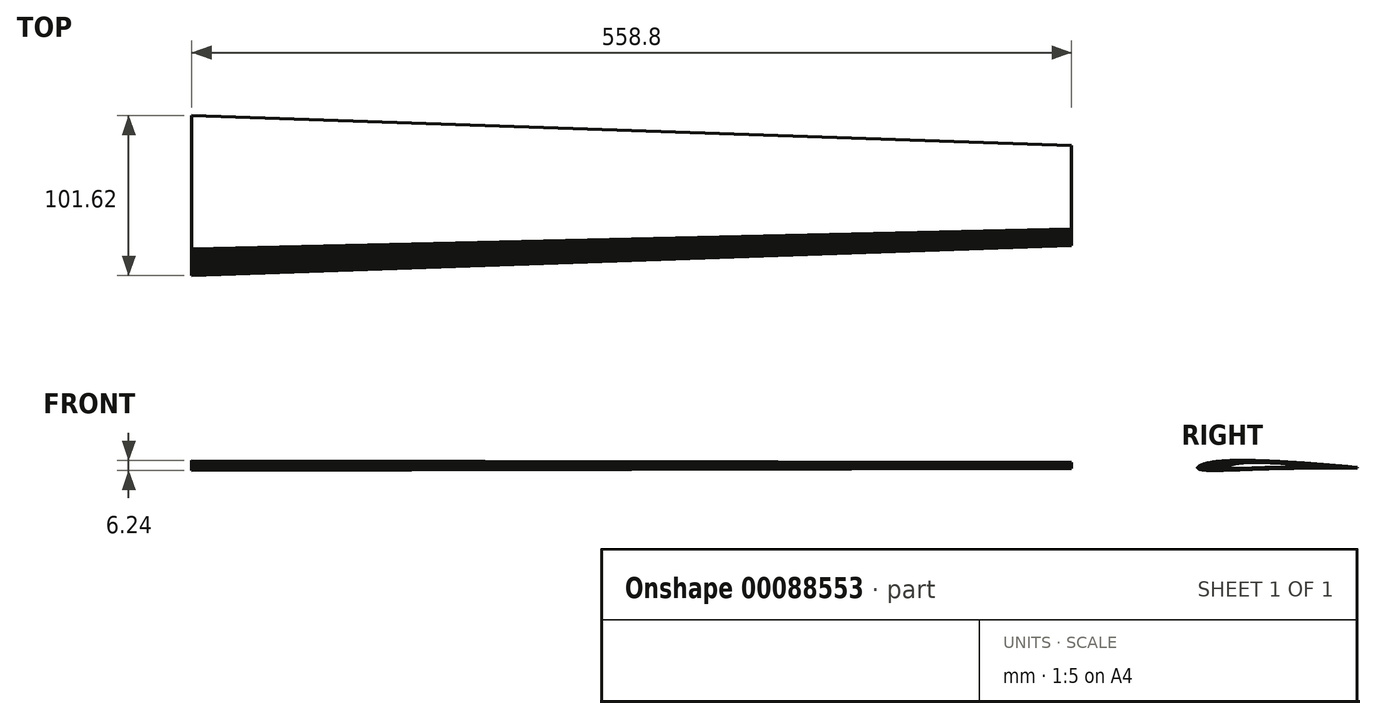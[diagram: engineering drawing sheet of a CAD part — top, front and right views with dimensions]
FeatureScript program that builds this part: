
annotation { "Feature Type Name" : "Feature", "Feature Type Description" : "" }
export const myFeature = defineFeature(function(context is Context, id is Id, definition is map)
    precondition{}
    {
        {
            var Q0;
            Q0=qCreatedBy(makeId("Right.planeOp"),FACE);
            var sketch = newSketch(context, id + "F0", { "sketchPlane" : qUnion([Q0])});
            skLineSegment(sketch, "E0", {"start": v(50.8, -1.4) * mm, "end": v(50.35, -1.36) * mm});
            skLineSegment(sketch, "E1", {"start": v(50.35, -1.36) * mm, "end": v(49.4, -1.27) * mm});
            skLineSegment(sketch, "E2", {"start": v(49.4, -1.27) * mm, "end": v(48.24, -1.16) * mm});
            skLineSegment(sketch, "E3", {"start": v(48.24, -1.16) * mm, "end": v(46.98, -1.04) * mm});
            skLineSegment(sketch, "E4", {"start": v(46.98, -1.04) * mm, "end": v(45.68, -0.91) * mm});
            skLineSegment(sketch, "E5", {"start": v(45.68, -0.91) * mm, "end": v(44.37, -0.8) * mm});
            skLineSegment(sketch, "E6", {"start": v(44.37, -0.8) * mm, "end": v(43.06, -0.67) * mm});
            skLineSegment(sketch, "E7", {"start": v(43.06, -0.67) * mm, "end": v(41.75, -0.55) * mm});
            skLineSegment(sketch, "E8", {"start": v(41.75, -0.55) * mm, "end": v(40.44, -0.43) * mm});
            skLineSegment(sketch, "E9", {"start": v(40.44, -0.43) * mm, "end": v(39.13, -0.32) * mm});
            skLineSegment(sketch, "E10", {"start": v(39.13, -0.32) * mm, "end": v(37.82, -0.2) * mm});
            skLineSegment(sketch, "E11", {"start": v(37.82, -0.2) * mm, "end": v(36.51, -0.1) * mm});
            skLineSegment(sketch, "E12", {"start": v(36.51, -0.1) * mm, "end": v(35.2, 0.02) * mm});
            skLineSegment(sketch, "E13", {"start": v(35.2, 0.02) * mm, "end": v(33.89, 0.13) * mm});
            skLineSegment(sketch, "E14", {"start": v(33.89, 0.13) * mm, "end": v(32.58, 0.24) * mm});
            skLineSegment(sketch, "E15", {"start": v(32.58, 0.24) * mm, "end": v(31.26, 0.35) * mm});
            skLineSegment(sketch, "E16", {"start": v(31.26, 0.35) * mm, "end": v(29.95, 0.45) * mm});
            skLineSegment(sketch, "E17", {"start": v(29.95, 0.45) * mm, "end": v(28.64, 0.56) * mm});
            skLineSegment(sketch, "E18", {"start": v(28.64, 0.56) * mm, "end": v(27.33, 0.66) * mm});
            skLineSegment(sketch, "E19", {"start": v(27.33, 0.66) * mm, "end": v(26.01, 0.76) * mm});
            skLineSegment(sketch, "E20", {"start": v(26.01, 0.76) * mm, "end": v(24.7, 0.87) * mm});
            skLineSegment(sketch, "E21", {"start": v(24.7, 0.87) * mm, "end": v(23.39, 0.96) * mm});
            skLineSegment(sketch, "E22", {"start": v(23.39, 0.96) * mm, "end": v(22.08, 1.06) * mm});
            skLineSegment(sketch, "E23", {"start": v(22.08, 1.06) * mm, "end": v(20.76, 1.16) * mm});
            skLineSegment(sketch, "E24", {"start": v(20.76, 1.16) * mm, "end": v(19.45, 1.25) * mm});
            skLineSegment(sketch, "E25", {"start": v(19.45, 1.25) * mm, "end": v(18.14, 1.35) * mm});
            skLineSegment(sketch, "E26", {"start": v(18.14, 1.35) * mm, "end": v(16.83, 1.44) * mm});
            skLineSegment(sketch, "E27", {"start": v(16.83, 1.44) * mm, "end": v(15.51, 1.53) * mm});
            skLineSegment(sketch, "E28", {"start": v(15.51, 1.53) * mm, "end": v(14.2, 1.62) * mm});
            skLineSegment(sketch, "E29", {"start": v(14.2, 1.62) * mm, "end": v(12.9, 1.7) * mm});
            skLineSegment(sketch, "E30", {"start": v(12.9, 1.7) * mm, "end": v(11.58, 1.8) * mm});
            skLineSegment(sketch, "E31", {"start": v(11.58, 1.8) * mm, "end": v(10.27, 1.88) * mm});
            skLineSegment(sketch, "E32", {"start": v(10.27, 1.88) * mm, "end": v(8.96, 1.96) * mm});
            skLineSegment(sketch, "E33", {"start": v(8.96, 1.96) * mm, "end": v(7.65, 2.04) * mm});
            skLineSegment(sketch, "E34", {"start": v(7.65, 2.04) * mm, "end": v(6.34, 2.12) * mm});
            skLineSegment(sketch, "E35", {"start": v(6.34, 2.12) * mm, "end": v(5.03, 2.2) * mm});
            skLineSegment(sketch, "E36", {"start": v(5.03, 2.2) * mm, "end": v(3.72, 2.26) * mm});
            skLineSegment(sketch, "E37", {"start": v(3.72, 2.26) * mm, "end": v(2.4, 2.33) * mm});
            skLineSegment(sketch, "E38", {"start": v(2.4, 2.33) * mm, "end": v(1.1, 2.4) * mm});
            skLineSegment(sketch, "E39", {"start": v(1.1, 2.4) * mm, "end": v(-0.21, 2.47) * mm});
            skLineSegment(sketch, "E40", {"start": v(-0.21, 2.47) * mm, "end": v(-1.52, 2.53) * mm});
            skLineSegment(sketch, "E41", {"start": v(-1.52, 2.53) * mm, "end": v(-2.83, 2.6) * mm});
            skLineSegment(sketch, "E42", {"start": v(-2.83, 2.6) * mm, "end": v(-4.14, 2.65) * mm});
            skLineSegment(sketch, "E43", {"start": v(-4.14, 2.65) * mm, "end": v(-5.45, 2.7) * mm});
            skLineSegment(sketch, "E44", {"start": v(-5.45, 2.7) * mm, "end": v(-6.76, 2.76) * mm});
            skLineSegment(sketch, "E45", {"start": v(-6.76, 2.76) * mm, "end": v(-8.07, 2.81) * mm});
            skLineSegment(sketch, "E46", {"start": v(-8.07, 2.81) * mm, "end": v(-9.37, 2.86) * mm});
            skLineSegment(sketch, "E47", {"start": v(-9.37, 2.86) * mm, "end": v(-10.68, 2.9) * mm});
            skLineSegment(sketch, "E48", {"start": v(-10.68, 2.9) * mm, "end": v(-11.98, 2.94) * mm});
            skLineSegment(sketch, "E49", {"start": v(-11.98, 2.94) * mm, "end": v(-13.29, 2.98) * mm});
            skLineSegment(sketch, "E50", {"start": v(-13.29, 2.98) * mm, "end": v(-14.6, 3.01) * mm});
            skLineSegment(sketch, "E51", {"start": v(-14.6, 3.01) * mm, "end": v(-15.9, 3.04) * mm});
            skLineSegment(sketch, "E52", {"start": v(-15.9, 3.04) * mm, "end": v(-17.2, 3.07) * mm});
            skLineSegment(sketch, "E53", {"start": v(-17.2, 3.07) * mm, "end": v(-18.5, 3.09) * mm});
            skLineSegment(sketch, "E54", {"start": v(-18.5, 3.09) * mm, "end": v(-19.8, 3.1) * mm});
            skLineSegment(sketch, "E55", {"start": v(-19.8, 3.1) * mm, "end": v(-21.1, 3.12) * mm});
            skLineSegment(sketch, "E56", {"start": v(-21.1, 3.12) * mm, "end": v(-22.39, 3.12) * mm});
            skLineSegment(sketch, "E57", {"start": v(-22.39, 3.12) * mm, "end": v(-23.68, 3.12) * mm});
            skLineSegment(sketch, "E58", {"start": v(-23.68, 3.12) * mm, "end": v(-24.97, 3.12) * mm});
            skLineSegment(sketch, "E59", {"start": v(-24.97, 3.12) * mm, "end": v(-26.25, 3.1) * mm});
            skLineSegment(sketch, "E60", {"start": v(-26.25, 3.1) * mm, "end": v(-27.53, 3.08) * mm});
            skLineSegment(sketch, "E61", {"start": v(-27.53, 3.08) * mm, "end": v(-28.81, 3.05) * mm});
            skLineSegment(sketch, "E62", {"start": v(-28.81, 3.05) * mm, "end": v(-30.09, 3.01) * mm});
            skLineSegment(sketch, "E63", {"start": v(-30.09, 3.01) * mm, "end": v(-31.35, 2.96) * mm});
            skLineSegment(sketch, "E64", {"start": v(-31.35, 2.96) * mm, "end": v(-32.62, 2.9) * mm});
            skLineSegment(sketch, "E65", {"start": v(-32.62, 2.9) * mm, "end": v(-33.88, 2.84) * mm});
            skLineSegment(sketch, "E66", {"start": v(-33.88, 2.84) * mm, "end": v(-35.12, 2.75) * mm});
            skLineSegment(sketch, "E67", {"start": v(-35.12, 2.75) * mm, "end": v(-36.36, 2.66) * mm});
            skLineSegment(sketch, "E68", {"start": v(-36.36, 2.66) * mm, "end": v(-37.6, 2.55) * mm});
            skLineSegment(sketch, "E69", {"start": v(-37.6, 2.55) * mm, "end": v(-38.81, 2.42) * mm});
            skLineSegment(sketch, "E70", {"start": v(-38.81, 2.42) * mm, "end": v(-40.01, 2.28) * mm});
            skLineSegment(sketch, "E71", {"start": v(-40.01, 2.28) * mm, "end": v(-41.2, 2.11) * mm});
            skLineSegment(sketch, "E72", {"start": v(-41.2, 2.11) * mm, "end": v(-42.37, 1.93) * mm});
            skLineSegment(sketch, "E73", {"start": v(-42.37, 1.93) * mm, "end": v(-43.5, 1.72) * mm});
            skLineSegment(sketch, "E74", {"start": v(-43.5, 1.72) * mm, "end": v(-44.61, 1.5) * mm});
            skLineSegment(sketch, "E75", {"start": v(-44.61, 1.5) * mm, "end": v(-45.67, 1.24) * mm});
            skLineSegment(sketch, "E76", {"start": v(-45.67, 1.24) * mm, "end": v(-46.67, 0.96) * mm});
            skLineSegment(sketch, "E77", {"start": v(-46.67, 0.96) * mm, "end": v(-47.57, 0.67) * mm});
            skLineSegment(sketch, "E78", {"start": v(-47.57, 0.67) * mm, "end": v(-48.34, 0.38) * mm});
            skLineSegment(sketch, "E79", {"start": v(-48.34, 0.38) * mm, "end": v(-48.96, 0.1) * mm});
            skLineSegment(sketch, "E80", {"start": v(-48.96, 0.1) * mm, "end": v(-49.44, -0.14) * mm});
            skLineSegment(sketch, "E81", {"start": v(-49.44, -0.14) * mm, "end": v(-49.8, -0.35) * mm});
            skLineSegment(sketch, "E82", {"start": v(-49.8, -0.35) * mm, "end": v(-50.07, -0.54) * mm});
            skLineSegment(sketch, "E83", {"start": v(-50.07, -0.54) * mm, "end": v(-50.28, -0.7) * mm});
            skLineSegment(sketch, "E84", {"start": v(-50.28, -0.7) * mm, "end": v(-50.45, -0.85) * mm});
            skLineSegment(sketch, "E85", {"start": v(-50.45, -0.85) * mm, "end": v(-50.58, -1) * mm});
            skLineSegment(sketch, "E86", {"start": v(-50.58, -1) * mm, "end": v(-50.68, -1.12) * mm});
            skLineSegment(sketch, "E87", {"start": v(-50.68, -1.12) * mm, "end": v(-50.75, -1.24) * mm});
            skLineSegment(sketch, "E88", {"start": v(-50.75, -1.24) * mm, "end": v(-50.8, -1.36) * mm});
            skLineSegment(sketch, "E89", {"start": v(-50.8, -1.36) * mm, "end": v(-50.8, -1.47) * mm});
            skLineSegment(sketch, "E90", {"start": v(-50.8, -1.47) * mm, "end": v(-50.8, -1.57) * mm});
            skLineSegment(sketch, "E91", {"start": v(-50.8, -1.57) * mm, "end": v(-50.77, -1.67) * mm});
            skLineSegment(sketch, "E92", {"start": v(-50.77, -1.67) * mm, "end": v(-50.7, -1.78) * mm});
            skLineSegment(sketch, "E93", {"start": v(-50.7, -1.78) * mm, "end": v(-50.6, -1.9) * mm});
            skLineSegment(sketch, "E94", {"start": v(-50.6, -1.9) * mm, "end": v(-50.47, -2) * mm});
            skLineSegment(sketch, "E95", {"start": v(-50.47, -2) * mm, "end": v(-50.3, -2.1) * mm});
            skLineSegment(sketch, "E96", {"start": v(-50.3, -2.1) * mm, "end": v(-50.1, -2.2) * mm});
            skLineSegment(sketch, "E97", {"start": v(-50.1, -2.2) * mm, "end": v(-49.86, -2.3) * mm});
            skLineSegment(sketch, "E98", {"start": v(-49.86, -2.3) * mm, "end": v(-49.54, -2.4) * mm});
            skLineSegment(sketch, "E99", {"start": v(-49.54, -2.4) * mm, "end": v(-49.14, -2.52) * mm});
            skLineSegment(sketch, "E100", {"start": v(-49.14, -2.52) * mm, "end": v(-48.6, -2.64) * mm});
            skLineSegment(sketch, "E101", {"start": v(-48.6, -2.64) * mm, "end": v(-47.88, -2.76) * mm});
            skLineSegment(sketch, "E102", {"start": v(-47.88, -2.76) * mm, "end": v(-47, -2.87) * mm});
            skLineSegment(sketch, "E103", {"start": v(-47, -2.87) * mm, "end": v(-45.96, -2.97) * mm});
            skLineSegment(sketch, "E104", {"start": v(-45.96, -2.97) * mm, "end": v(-44.84, -3.03) * mm});
            skLineSegment(sketch, "E105", {"start": v(-44.84, -3.03) * mm, "end": v(-43.66, -3.08) * mm});
            skLineSegment(sketch, "E106", {"start": v(-43.66, -3.08) * mm, "end": v(-42.44, -3.1) * mm});
            skLineSegment(sketch, "E107", {"start": v(-42.44, -3.1) * mm, "end": v(-41.2, -3.12) * mm});
            skLineSegment(sketch, "E108", {"start": v(-41.2, -3.12) * mm, "end": v(-39.93, -3.12) * mm});
            skLineSegment(sketch, "E109", {"start": v(-39.93, -3.12) * mm, "end": v(-38.66, -3.11) * mm});
            skLineSegment(sketch, "E110", {"start": v(-38.66, -3.11) * mm, "end": v(-37.37, -3.1) * mm});
            skLineSegment(sketch, "E111", {"start": v(-37.37, -3.1) * mm, "end": v(-36.08, -3.07) * mm});
            skLineSegment(sketch, "E112", {"start": v(-36.08, -3.07) * mm, "end": v(-34.78, -3.05) * mm});
            skLineSegment(sketch, "E113", {"start": v(-34.78, -3.05) * mm, "end": v(-33.47, -3.01) * mm});
            skLineSegment(sketch, "E114", {"start": v(-33.47, -3.01) * mm, "end": v(-32.16, -2.98) * mm});
            skLineSegment(sketch, "E115", {"start": v(-32.16, -2.98) * mm, "end": v(-30.84, -2.94) * mm});
            skLineSegment(sketch, "E116", {"start": v(-30.84, -2.94) * mm, "end": v(-29.52, -2.9) * mm});
            skLineSegment(sketch, "E117", {"start": v(-29.52, -2.9) * mm, "end": v(-28.2, -2.85) * mm});
            skLineSegment(sketch, "E118", {"start": v(-28.2, -2.85) * mm, "end": v(-26.88, -2.8) * mm});
            skLineSegment(sketch, "E119", {"start": v(-26.88, -2.8) * mm, "end": v(-25.56, -2.76) * mm});
            skLineSegment(sketch, "E120", {"start": v(-25.56, -2.76) * mm, "end": v(-24.24, -2.7) * mm});
            skLineSegment(sketch, "E121", {"start": v(-24.24, -2.7) * mm, "end": v(-22.92, -2.66) * mm});
            skLineSegment(sketch, "E122", {"start": v(-22.92, -2.66) * mm, "end": v(-21.6, -2.61) * mm});
            skLineSegment(sketch, "E123", {"start": v(-21.6, -2.61) * mm, "end": v(-20.3, -2.56) * mm});
            skLineSegment(sketch, "E124", {"start": v(-20.3, -2.56) * mm, "end": v(-18.98, -2.51) * mm});
            skLineSegment(sketch, "E125", {"start": v(-18.98, -2.51) * mm, "end": v(-17.67, -2.46) * mm});
            skLineSegment(sketch, "E126", {"start": v(-17.67, -2.46) * mm, "end": v(-16.35, -2.42) * mm});
            skLineSegment(sketch, "E127", {"start": v(-16.35, -2.42) * mm, "end": v(-15.04, -2.37) * mm});
            skLineSegment(sketch, "E128", {"start": v(-15.04, -2.37) * mm, "end": v(-13.73, -2.32) * mm});
            skLineSegment(sketch, "E129", {"start": v(-13.73, -2.32) * mm, "end": v(-12.41, -2.28) * mm});
            skLineSegment(sketch, "E130", {"start": v(-12.41, -2.28) * mm, "end": v(-11.1, -2.24) * mm});
            skLineSegment(sketch, "E131", {"start": v(-11.1, -2.24) * mm, "end": v(-9.79, -2.2) * mm});
            skLineSegment(sketch, "E132", {"start": v(-9.79, -2.2) * mm, "end": v(-8.47, -2.15) * mm});
            skLineSegment(sketch, "E133", {"start": v(-8.47, -2.15) * mm, "end": v(-7.16, -2.11) * mm});
            skLineSegment(sketch, "E134", {"start": v(-7.16, -2.11) * mm, "end": v(-5.85, -2.08) * mm});
            skLineSegment(sketch, "E135", {"start": v(-5.85, -2.08) * mm, "end": v(-4.53, -2.04) * mm});
            skLineSegment(sketch, "E136", {"start": v(-4.53, -2.04) * mm, "end": v(-3.22, -2) * mm});
            skLineSegment(sketch, "E137", {"start": v(-3.22, -2) * mm, "end": v(-1.9, -1.97) * mm});
            skLineSegment(sketch, "E138", {"start": v(-1.9, -1.97) * mm, "end": v(-0.59, -1.94) * mm});
            skLineSegment(sketch, "E139", {"start": v(-0.59, -1.94) * mm, "end": v(0.73, -1.91) * mm});
            skLineSegment(sketch, "E140", {"start": v(0.73, -1.91) * mm, "end": v(2.04, -1.89) * mm});
            skLineSegment(sketch, "E141", {"start": v(2.04, -1.89) * mm, "end": v(3.36, -1.86) * mm});
            skLineSegment(sketch, "E142", {"start": v(3.36, -1.86) * mm, "end": v(4.67, -1.84) * mm});
            skLineSegment(sketch, "E143", {"start": v(4.67, -1.84) * mm, "end": v(6, -1.82) * mm});
            skLineSegment(sketch, "E144", {"start": v(6, -1.82) * mm, "end": v(7.31, -1.8) * mm});
            skLineSegment(sketch, "E145", {"start": v(7.31, -1.8) * mm, "end": v(8.63, -1.78) * mm});
            skLineSegment(sketch, "E146", {"start": v(8.63, -1.78) * mm, "end": v(9.95, -1.76) * mm});
            skLineSegment(sketch, "E147", {"start": v(9.95, -1.76) * mm, "end": v(11.27, -1.74) * mm});
            skLineSegment(sketch, "E148", {"start": v(11.27, -1.74) * mm, "end": v(12.6, -1.73) * mm});
            skLineSegment(sketch, "E149", {"start": v(12.6, -1.73) * mm, "end": v(13.9, -1.72) * mm});
            skLineSegment(sketch, "E150", {"start": v(13.9, -1.72) * mm, "end": v(15.23, -1.7) * mm});
            skLineSegment(sketch, "E151", {"start": v(15.23, -1.7) * mm, "end": v(16.55, -1.7) * mm});
            skLineSegment(sketch, "E152", {"start": v(16.55, -1.7) * mm, "end": v(17.87, -1.69) * mm});
            skLineSegment(sketch, "E153", {"start": v(17.87, -1.69) * mm, "end": v(19.2, -1.68) * mm});
            skLineSegment(sketch, "E154", {"start": v(19.2, -1.68) * mm, "end": v(20.52, -1.67) * mm});
            skLineSegment(sketch, "E155", {"start": v(20.52, -1.67) * mm, "end": v(21.84, -1.67) * mm});
            skLineSegment(sketch, "E156", {"start": v(21.84, -1.67) * mm, "end": v(23.16, -1.66) * mm});
            skLineSegment(sketch, "E157", {"start": v(23.16, -1.66) * mm, "end": v(24.48, -1.66) * mm});
            skLineSegment(sketch, "E158", {"start": v(24.48, -1.66) * mm, "end": v(25.8, -1.65) * mm});
            skLineSegment(sketch, "E159", {"start": v(25.8, -1.65) * mm, "end": v(27.12, -1.65) * mm});
            skLineSegment(sketch, "E160", {"start": v(27.12, -1.65) * mm, "end": v(28.45, -1.64) * mm});
            skLineSegment(sketch, "E161", {"start": v(28.45, -1.64) * mm, "end": v(29.77, -1.64) * mm});
            skLineSegment(sketch, "E162", {"start": v(29.77, -1.64) * mm, "end": v(31.09, -1.63) * mm});
            skLineSegment(sketch, "E163", {"start": v(31.09, -1.63) * mm, "end": v(32.41, -1.63) * mm});
            skLineSegment(sketch, "E164", {"start": v(32.41, -1.63) * mm, "end": v(33.74, -1.63) * mm});
            skLineSegment(sketch, "E165", {"start": v(33.74, -1.63) * mm, "end": v(35.06, -1.62) * mm});
            skLineSegment(sketch, "E166", {"start": v(35.06, -1.62) * mm, "end": v(36.38, -1.62) * mm});
            skLineSegment(sketch, "E167", {"start": v(36.38, -1.62) * mm, "end": v(37.7, -1.62) * mm});
            skLineSegment(sketch, "E168", {"start": v(37.7, -1.62) * mm, "end": v(39.03, -1.61) * mm});
            skLineSegment(sketch, "E169", {"start": v(39.03, -1.61) * mm, "end": v(40.35, -1.6) * mm});
            skLineSegment(sketch, "E170", {"start": v(40.35, -1.6) * mm, "end": v(41.67, -1.6) * mm});
            skLineSegment(sketch, "E171", {"start": v(41.67, -1.6) * mm, "end": v(43, -1.6) * mm});
            skLineSegment(sketch, "E172", {"start": v(43, -1.6) * mm, "end": v(44.32, -1.6) * mm});
            skLineSegment(sketch, "E173", {"start": v(44.32, -1.6) * mm, "end": v(45.64, -1.59) * mm});
            skLineSegment(sketch, "E174", {"start": v(45.64, -1.59) * mm, "end": v(46.95, -1.59) * mm});
            skLineSegment(sketch, "E175", {"start": v(46.95, -1.59) * mm, "end": v(48.22, -1.58) * mm});
            skLineSegment(sketch, "E176", {"start": v(48.22, -1.58) * mm, "end": v(49.4, -1.58) * mm});
            skLineSegment(sketch, "E177", {"start": v(49.4, -1.58) * mm, "end": v(50.35, -1.57) * mm});
            skLineSegment(sketch, "E178", {"start": v(50.35, -1.57) * mm, "end": v(50.8, -1.57) * mm});
            skLineSegment(sketch, "E179", {"start": v(50.8, -1.57) * mm, "end": v(50.8, -1.4) * mm});
            skSolve(sketch);
        }
        {
            var Q0;
            Q0=qCreatedBy(makeId("Right.planeOp"),FACE);
            cPlane(context, id + "F1", {"entities" : qUnion([Q0]), "cplaneType" : CPlaneType.OFFSET, "offset" : 558.8 * mm, "width" : 152.4 * mm, "height" : 152.4 * mm});
        }
        {
            var Q0;
            Q0=qCreatedBy(id+"F1.planeOp",FACE);
            var sketch = newSketch(context, id + "F2", { "sketchPlane" : qUnion([Q0])});
            skLineSegment(sketch, "E180", {"start": v(31.75, -0.88) * mm, "end": v(31.47, -0.85) * mm});
            skLineSegment(sketch, "E181", {"start": v(31.47, -0.85) * mm, "end": v(30.87, -0.8) * mm});
            skLineSegment(sketch, "E182", {"start": v(30.87, -0.8) * mm, "end": v(30.14, -0.72) * mm});
            skLineSegment(sketch, "E183", {"start": v(30.14, -0.72) * mm, "end": v(29.36, -0.65) * mm});
            skLineSegment(sketch, "E184", {"start": v(29.36, -0.65) * mm, "end": v(28.54, -0.57) * mm});
            skLineSegment(sketch, "E185", {"start": v(28.54, -0.57) * mm, "end": v(27.73, -0.5) * mm});
            skLineSegment(sketch, "E186", {"start": v(27.73, -0.5) * mm, "end": v(26.9, -0.42) * mm});
            skLineSegment(sketch, "E187", {"start": v(26.9, -0.42) * mm, "end": v(26.1, -0.35) * mm});
            skLineSegment(sketch, "E188", {"start": v(26.1, -0.35) * mm, "end": v(25.27, -0.27) * mm});
            skLineSegment(sketch, "E189", {"start": v(25.27, -0.27) * mm, "end": v(24.45, -0.2) * mm});
            skLineSegment(sketch, "E190", {"start": v(24.45, -0.2) * mm, "end": v(23.63, -0.13) * mm});
            skLineSegment(sketch, "E191", {"start": v(23.63, -0.13) * mm, "end": v(22.82, -0.06) * mm});
            skLineSegment(sketch, "E192", {"start": v(22.82, -0.06) * mm, "end": v(22, 0.01) * mm});
            skLineSegment(sketch, "E193", {"start": v(22, 0.01) * mm, "end": v(21.18, 0.08) * mm});
            skLineSegment(sketch, "E194", {"start": v(21.18, 0.08) * mm, "end": v(20.36, 0.15) * mm});
            skLineSegment(sketch, "E195", {"start": v(20.36, 0.15) * mm, "end": v(19.54, 0.22) * mm});
            skLineSegment(sketch, "E196", {"start": v(19.54, 0.22) * mm, "end": v(18.72, 0.28) * mm});
            skLineSegment(sketch, "E197", {"start": v(18.72, 0.28) * mm, "end": v(17.9, 0.35) * mm});
            skLineSegment(sketch, "E198", {"start": v(17.9, 0.35) * mm, "end": v(17.08, 0.41) * mm});
            skLineSegment(sketch, "E199", {"start": v(17.08, 0.41) * mm, "end": v(16.26, 0.48) * mm});
            skLineSegment(sketch, "E200", {"start": v(16.26, 0.48) * mm, "end": v(15.44, 0.54) * mm});
            skLineSegment(sketch, "E201", {"start": v(15.44, 0.54) * mm, "end": v(14.62, 0.6) * mm});
            skLineSegment(sketch, "E202", {"start": v(14.62, 0.6) * mm, "end": v(13.8, 0.66) * mm});
            skLineSegment(sketch, "E203", {"start": v(13.8, 0.66) * mm, "end": v(12.98, 0.72) * mm});
            skLineSegment(sketch, "E204", {"start": v(12.98, 0.72) * mm, "end": v(12.16, 0.78) * mm});
            skLineSegment(sketch, "E205", {"start": v(12.16, 0.78) * mm, "end": v(11.34, 0.84) * mm});
            skLineSegment(sketch, "E206", {"start": v(11.34, 0.84) * mm, "end": v(10.52, 0.9) * mm});
            skLineSegment(sketch, "E207", {"start": v(10.52, 0.9) * mm, "end": v(9.7, 0.96) * mm});
            skLineSegment(sketch, "E208", {"start": v(9.7, 0.96) * mm, "end": v(8.88, 1.01) * mm});
            skLineSegment(sketch, "E209", {"start": v(8.88, 1.01) * mm, "end": v(8.06, 1.07) * mm});
            skLineSegment(sketch, "E210", {"start": v(8.06, 1.07) * mm, "end": v(7.24, 1.12) * mm});
            skLineSegment(sketch, "E211", {"start": v(7.24, 1.12) * mm, "end": v(6.42, 1.17) * mm});
            skLineSegment(sketch, "E212", {"start": v(6.42, 1.17) * mm, "end": v(5.6, 1.22) * mm});
            skLineSegment(sketch, "E213", {"start": v(5.6, 1.22) * mm, "end": v(4.78, 1.27) * mm});
            skLineSegment(sketch, "E214", {"start": v(4.78, 1.27) * mm, "end": v(3.96, 1.32) * mm});
            skLineSegment(sketch, "E215", {"start": v(3.96, 1.32) * mm, "end": v(3.14, 1.37) * mm});
            skLineSegment(sketch, "E216", {"start": v(3.14, 1.37) * mm, "end": v(2.32, 1.41) * mm});
            skLineSegment(sketch, "E217", {"start": v(2.32, 1.41) * mm, "end": v(1.5, 1.46) * mm});
            skLineSegment(sketch, "E218", {"start": v(1.5, 1.46) * mm, "end": v(0.68, 1.5) * mm});
            skLineSegment(sketch, "E219", {"start": v(0.68, 1.5) * mm, "end": v(-0.13, 1.54) * mm});
            skLineSegment(sketch, "E220", {"start": v(-0.13, 1.54) * mm, "end": v(-0.95, 1.58) * mm});
            skLineSegment(sketch, "E221", {"start": v(-0.95, 1.58) * mm, "end": v(-1.77, 1.62) * mm});
            skLineSegment(sketch, "E222", {"start": v(-1.77, 1.62) * mm, "end": v(-2.59, 1.66) * mm});
            skLineSegment(sketch, "E223", {"start": v(-2.59, 1.66) * mm, "end": v(-3.4, 1.7) * mm});
            skLineSegment(sketch, "E224", {"start": v(-3.4, 1.7) * mm, "end": v(-4.22, 1.73) * mm});
            skLineSegment(sketch, "E225", {"start": v(-4.22, 1.73) * mm, "end": v(-5.04, 1.76) * mm});
            skLineSegment(sketch, "E226", {"start": v(-5.04, 1.76) * mm, "end": v(-5.86, 1.79) * mm});
            skLineSegment(sketch, "E227", {"start": v(-5.86, 1.79) * mm, "end": v(-6.67, 1.81) * mm});
            skLineSegment(sketch, "E228", {"start": v(-6.67, 1.81) * mm, "end": v(-7.49, 1.84) * mm});
            skLineSegment(sketch, "E229", {"start": v(-7.49, 1.84) * mm, "end": v(-8.3, 1.86) * mm});
            skLineSegment(sketch, "E230", {"start": v(-8.3, 1.86) * mm, "end": v(-9.12, 1.88) * mm});
            skLineSegment(sketch, "E231", {"start": v(-9.12, 1.88) * mm, "end": v(-9.93, 1.9) * mm});
            skLineSegment(sketch, "E232", {"start": v(-9.93, 1.9) * mm, "end": v(-10.75, 1.92) * mm});
            skLineSegment(sketch, "E233", {"start": v(-10.75, 1.92) * mm, "end": v(-11.56, 1.93) * mm});
            skLineSegment(sketch, "E234", {"start": v(-11.56, 1.93) * mm, "end": v(-12.37, 1.94) * mm});
            skLineSegment(sketch, "E235", {"start": v(-12.37, 1.94) * mm, "end": v(-13.18, 1.95) * mm});
            skLineSegment(sketch, "E236", {"start": v(-13.18, 1.95) * mm, "end": v(-13.99, 1.95) * mm});
            skLineSegment(sketch, "E237", {"start": v(-13.99, 1.95) * mm, "end": v(-14.8, 1.95) * mm});
            skLineSegment(sketch, "E238", {"start": v(-14.8, 1.95) * mm, "end": v(-15.6, 1.95) * mm});
            skLineSegment(sketch, "E239", {"start": v(-15.6, 1.95) * mm, "end": v(-16.4, 1.94) * mm});
            skLineSegment(sketch, "E240", {"start": v(-16.4, 1.94) * mm, "end": v(-17.2, 1.92) * mm});
            skLineSegment(sketch, "E241", {"start": v(-17.2, 1.92) * mm, "end": v(-18, 1.9) * mm});
            skLineSegment(sketch, "E242", {"start": v(-18, 1.9) * mm, "end": v(-18.8, 1.88) * mm});
            skLineSegment(sketch, "E243", {"start": v(-18.8, 1.88) * mm, "end": v(-19.6, 1.85) * mm});
            skLineSegment(sketch, "E244", {"start": v(-19.6, 1.85) * mm, "end": v(-20.38, 1.82) * mm});
            skLineSegment(sketch, "E245", {"start": v(-20.38, 1.82) * mm, "end": v(-21.17, 1.77) * mm});
            skLineSegment(sketch, "E246", {"start": v(-21.17, 1.77) * mm, "end": v(-21.95, 1.72) * mm});
            skLineSegment(sketch, "E247", {"start": v(-21.95, 1.72) * mm, "end": v(-22.72, 1.66) * mm});
            skLineSegment(sketch, "E248", {"start": v(-22.72, 1.66) * mm, "end": v(-23.5, 1.6) * mm});
            skLineSegment(sketch, "E249", {"start": v(-23.5, 1.6) * mm, "end": v(-24.25, 1.51) * mm});
            skLineSegment(sketch, "E250", {"start": v(-24.25, 1.51) * mm, "end": v(-25, 1.42) * mm});
            skLineSegment(sketch, "E251", {"start": v(-25, 1.42) * mm, "end": v(-25.75, 1.32) * mm});
            skLineSegment(sketch, "E252", {"start": v(-25.75, 1.32) * mm, "end": v(-26.47, 1.2) * mm});
            skLineSegment(sketch, "E253", {"start": v(-26.47, 1.2) * mm, "end": v(-27.19, 1.08) * mm});
            skLineSegment(sketch, "E254", {"start": v(-27.19, 1.08) * mm, "end": v(-27.88, 0.93) * mm});
            skLineSegment(sketch, "E255", {"start": v(-27.88, 0.93) * mm, "end": v(-28.54, 0.77) * mm});
            skLineSegment(sketch, "E256", {"start": v(-28.54, 0.77) * mm, "end": v(-29.16, 0.6) * mm});
            skLineSegment(sketch, "E257", {"start": v(-29.16, 0.6) * mm, "end": v(-29.73, 0.42) * mm});
            skLineSegment(sketch, "E258", {"start": v(-29.73, 0.42) * mm, "end": v(-30.2, 0.24) * mm});
            skLineSegment(sketch, "E259", {"start": v(-30.2, 0.24) * mm, "end": v(-30.6, 0.07) * mm});
            skLineSegment(sketch, "E260", {"start": v(-30.6, 0.07) * mm, "end": v(-30.9, -0.09) * mm});
            skLineSegment(sketch, "E261", {"start": v(-30.9, -0.09) * mm, "end": v(-31.12, -0.22) * mm});
            skLineSegment(sketch, "E262", {"start": v(-31.12, -0.22) * mm, "end": v(-31.29, -0.34) * mm});
            skLineSegment(sketch, "E263", {"start": v(-31.29, -0.34) * mm, "end": v(-31.42, -0.44) * mm});
            skLineSegment(sketch, "E264", {"start": v(-31.42, -0.44) * mm, "end": v(-31.52, -0.53) * mm});
            skLineSegment(sketch, "E265", {"start": v(-31.52, -0.53) * mm, "end": v(-31.6, -0.62) * mm});
            skLineSegment(sketch, "E266", {"start": v(-31.6, -0.62) * mm, "end": v(-31.67, -0.7) * mm});
            skLineSegment(sketch, "E267", {"start": v(-31.67, -0.7) * mm, "end": v(-31.71, -0.78) * mm});
            skLineSegment(sketch, "E268", {"start": v(-31.71, -0.78) * mm, "end": v(-31.74, -0.85) * mm});
            skLineSegment(sketch, "E269", {"start": v(-31.74, -0.85) * mm, "end": v(-31.75, -0.92) * mm});
            skLineSegment(sketch, "E270", {"start": v(-31.75, -0.92) * mm, "end": v(-31.75, -0.98) * mm});
            skLineSegment(sketch, "E271", {"start": v(-31.75, -0.98) * mm, "end": v(-31.72, -1.05) * mm});
            skLineSegment(sketch, "E272", {"start": v(-31.72, -1.05) * mm, "end": v(-31.68, -1.11) * mm});
            skLineSegment(sketch, "E273", {"start": v(-31.68, -1.11) * mm, "end": v(-31.62, -1.18) * mm});
            skLineSegment(sketch, "E274", {"start": v(-31.62, -1.18) * mm, "end": v(-31.54, -1.25) * mm});
            skLineSegment(sketch, "E275", {"start": v(-31.54, -1.25) * mm, "end": v(-31.44, -1.3) * mm});
            skLineSegment(sketch, "E276", {"start": v(-31.44, -1.3) * mm, "end": v(-31.31, -1.37) * mm});
            skLineSegment(sketch, "E277", {"start": v(-31.31, -1.37) * mm, "end": v(-31.16, -1.44) * mm});
            skLineSegment(sketch, "E278", {"start": v(-31.16, -1.44) * mm, "end": v(-30.96, -1.5) * mm});
            skLineSegment(sketch, "E279", {"start": v(-30.96, -1.5) * mm, "end": v(-30.7, -1.58) * mm});
            skLineSegment(sketch, "E280", {"start": v(-30.7, -1.58) * mm, "end": v(-30.37, -1.65) * mm});
            skLineSegment(sketch, "E281", {"start": v(-30.37, -1.65) * mm, "end": v(-29.92, -1.73) * mm});
            skLineSegment(sketch, "E282", {"start": v(-29.92, -1.73) * mm, "end": v(-29.37, -1.8) * mm});
            skLineSegment(sketch, "E283", {"start": v(-29.37, -1.8) * mm, "end": v(-28.72, -1.85) * mm});
            skLineSegment(sketch, "E284", {"start": v(-28.72, -1.85) * mm, "end": v(-28.02, -1.9) * mm});
            skLineSegment(sketch, "E285", {"start": v(-28.02, -1.9) * mm, "end": v(-27.28, -1.92) * mm});
            skLineSegment(sketch, "E286", {"start": v(-27.28, -1.92) * mm, "end": v(-26.52, -1.94) * mm});
            skLineSegment(sketch, "E287", {"start": v(-26.52, -1.94) * mm, "end": v(-25.74, -1.95) * mm});
            skLineSegment(sketch, "E288", {"start": v(-25.74, -1.95) * mm, "end": v(-24.95, -1.95) * mm});
            skLineSegment(sketch, "E289", {"start": v(-24.95, -1.95) * mm, "end": v(-24.16, -1.95) * mm});
            skLineSegment(sketch, "E290", {"start": v(-24.16, -1.95) * mm, "end": v(-23.35, -1.94) * mm});
            skLineSegment(sketch, "E291", {"start": v(-23.35, -1.94) * mm, "end": v(-22.55, -1.92) * mm});
            skLineSegment(sketch, "E292", {"start": v(-22.55, -1.92) * mm, "end": v(-21.73, -1.9) * mm});
            skLineSegment(sketch, "E293", {"start": v(-21.73, -1.9) * mm, "end": v(-20.91, -1.88) * mm});
            skLineSegment(sketch, "E294", {"start": v(-20.91, -1.88) * mm, "end": v(-20.1, -1.86) * mm});
            skLineSegment(sketch, "E295", {"start": v(-20.1, -1.86) * mm, "end": v(-19.27, -1.83) * mm});
            skLineSegment(sketch, "E296", {"start": v(-19.27, -1.83) * mm, "end": v(-18.45, -1.8) * mm});
            skLineSegment(sketch, "E297", {"start": v(-18.45, -1.8) * mm, "end": v(-17.62, -1.78) * mm});
            skLineSegment(sketch, "E298", {"start": v(-17.62, -1.78) * mm, "end": v(-16.8, -1.75) * mm});
            skLineSegment(sketch, "E299", {"start": v(-16.8, -1.75) * mm, "end": v(-15.97, -1.72) * mm});
            skLineSegment(sketch, "E300", {"start": v(-15.97, -1.72) * mm, "end": v(-15.15, -1.7) * mm});
            skLineSegment(sketch, "E301", {"start": v(-15.15, -1.7) * mm, "end": v(-14.33, -1.66) * mm});
            skLineSegment(sketch, "E302", {"start": v(-14.33, -1.66) * mm, "end": v(-13.5, -1.63) * mm});
            skLineSegment(sketch, "E303", {"start": v(-13.5, -1.63) * mm, "end": v(-12.68, -1.6) * mm});
            skLineSegment(sketch, "E304", {"start": v(-12.68, -1.6) * mm, "end": v(-11.86, -1.57) * mm});
            skLineSegment(sketch, "E305", {"start": v(-11.86, -1.57) * mm, "end": v(-11.04, -1.54) * mm});
            skLineSegment(sketch, "E306", {"start": v(-11.04, -1.54) * mm, "end": v(-10.22, -1.5) * mm});
            skLineSegment(sketch, "E307", {"start": v(-10.22, -1.5) * mm, "end": v(-9.4, -1.48) * mm});
            skLineSegment(sketch, "E308", {"start": v(-9.4, -1.48) * mm, "end": v(-8.58, -1.45) * mm});
            skLineSegment(sketch, "E309", {"start": v(-8.58, -1.45) * mm, "end": v(-7.76, -1.42) * mm});
            skLineSegment(sketch, "E310", {"start": v(-7.76, -1.42) * mm, "end": v(-6.94, -1.4) * mm});
            skLineSegment(sketch, "E311", {"start": v(-6.94, -1.4) * mm, "end": v(-6.12, -1.37) * mm});
            skLineSegment(sketch, "E312", {"start": v(-6.12, -1.37) * mm, "end": v(-5.3, -1.34) * mm});
            skLineSegment(sketch, "E313", {"start": v(-5.3, -1.34) * mm, "end": v(-4.47, -1.32) * mm});
            skLineSegment(sketch, "E314", {"start": v(-4.47, -1.32) * mm, "end": v(-3.65, -1.3) * mm});
            skLineSegment(sketch, "E315", {"start": v(-3.65, -1.3) * mm, "end": v(-2.83, -1.27) * mm});
            skLineSegment(sketch, "E316", {"start": v(-2.83, -1.27) * mm, "end": v(-2.01, -1.25) * mm});
            skLineSegment(sketch, "E317", {"start": v(-2.01, -1.25) * mm, "end": v(-1.19, -1.23) * mm});
            skLineSegment(sketch, "E318", {"start": v(-1.19, -1.23) * mm, "end": v(-0.37, -1.21) * mm});
            skLineSegment(sketch, "E319", {"start": v(-0.37, -1.21) * mm, "end": v(0.45, -1.2) * mm});
            skLineSegment(sketch, "E320", {"start": v(0.45, -1.2) * mm, "end": v(1.28, -1.18) * mm});
            skLineSegment(sketch, "E321", {"start": v(1.28, -1.18) * mm, "end": v(2.1, -1.16) * mm});
            skLineSegment(sketch, "E322", {"start": v(2.1, -1.16) * mm, "end": v(2.92, -1.15) * mm});
            skLineSegment(sketch, "E323", {"start": v(2.92, -1.15) * mm, "end": v(3.75, -1.13) * mm});
            skLineSegment(sketch, "E324", {"start": v(3.75, -1.13) * mm, "end": v(4.57, -1.12) * mm});
            skLineSegment(sketch, "E325", {"start": v(4.57, -1.12) * mm, "end": v(5.4, -1.11) * mm});
            skLineSegment(sketch, "E326", {"start": v(5.4, -1.11) * mm, "end": v(6.22, -1.1) * mm});
            skLineSegment(sketch, "E327", {"start": v(6.22, -1.1) * mm, "end": v(7.04, -1.1) * mm});
            skLineSegment(sketch, "E328", {"start": v(7.04, -1.1) * mm, "end": v(7.87, -1.08) * mm});
            skLineSegment(sketch, "E329", {"start": v(7.87, -1.08) * mm, "end": v(8.7, -1.07) * mm});
            skLineSegment(sketch, "E330", {"start": v(8.7, -1.07) * mm, "end": v(9.52, -1.07) * mm});
            skLineSegment(sketch, "E331", {"start": v(9.52, -1.07) * mm, "end": v(10.34, -1.06) * mm});
            skLineSegment(sketch, "E332", {"start": v(10.34, -1.06) * mm, "end": v(11.17, -1.05) * mm});
            skLineSegment(sketch, "E333", {"start": v(11.17, -1.05) * mm, "end": v(12, -1.05) * mm});
            skLineSegment(sketch, "E334", {"start": v(12, -1.05) * mm, "end": v(12.82, -1.05) * mm});
            skLineSegment(sketch, "E335", {"start": v(12.82, -1.05) * mm, "end": v(13.65, -1.04) * mm});
            skLineSegment(sketch, "E336", {"start": v(13.65, -1.04) * mm, "end": v(14.47, -1.04) * mm});
            skLineSegment(sketch, "E337", {"start": v(14.47, -1.04) * mm, "end": v(15.3, -1.04) * mm});
            skLineSegment(sketch, "E338", {"start": v(15.3, -1.04) * mm, "end": v(16.12, -1.03) * mm});
            skLineSegment(sketch, "E339", {"start": v(16.12, -1.03) * mm, "end": v(16.95, -1.03) * mm});
            skLineSegment(sketch, "E340", {"start": v(16.95, -1.03) * mm, "end": v(17.78, -1.03) * mm});
            skLineSegment(sketch, "E341", {"start": v(17.78, -1.03) * mm, "end": v(18.6, -1.02) * mm});
            skLineSegment(sketch, "E342", {"start": v(18.6, -1.02) * mm, "end": v(19.43, -1.02) * mm});
            skLineSegment(sketch, "E343", {"start": v(19.43, -1.02) * mm, "end": v(20.25, -1.02) * mm});
            skLineSegment(sketch, "E344", {"start": v(20.25, -1.02) * mm, "end": v(21.08, -1.02) * mm});
            skLineSegment(sketch, "E345", {"start": v(21.08, -1.02) * mm, "end": v(21.9, -1.01) * mm});
            skLineSegment(sketch, "E346", {"start": v(21.9, -1.01) * mm, "end": v(22.73, -1.01) * mm});
            skLineSegment(sketch, "E347", {"start": v(22.73, -1.01) * mm, "end": v(23.56, -1) * mm});
            skLineSegment(sketch, "E348", {"start": v(23.56, -1) * mm, "end": v(24.39, -1) * mm});
            skLineSegment(sketch, "E349", {"start": v(24.39, -1) * mm, "end": v(25.21, -1) * mm});
            skLineSegment(sketch, "E350", {"start": v(25.21, -1) * mm, "end": v(26.04, -1) * mm});
            skLineSegment(sketch, "E351", {"start": v(26.04, -1) * mm, "end": v(26.87, -1) * mm});
            skLineSegment(sketch, "E352", {"start": v(26.87, -1) * mm, "end": v(27.7, -1) * mm});
            skLineSegment(sketch, "E353", {"start": v(27.7, -1) * mm, "end": v(28.52, -1) * mm});
            skLineSegment(sketch, "E354", {"start": v(28.52, -1) * mm, "end": v(29.34, -1) * mm});
            skLineSegment(sketch, "E355", {"start": v(29.34, -1) * mm, "end": v(30.13, -0.99) * mm});
            skLineSegment(sketch, "E356", {"start": v(30.13, -0.99) * mm, "end": v(30.87, -0.99) * mm});
            skLineSegment(sketch, "E357", {"start": v(30.87, -0.99) * mm, "end": v(31.46, -0.98) * mm});
            skLineSegment(sketch, "E358", {"start": v(31.46, -0.98) * mm, "end": v(31.75, -0.98) * mm});
            skLineSegment(sketch, "E359", {"start": v(31.75, -0.98) * mm, "end": v(31.75, -0.88) * mm});
            skSolve(sketch);
        }
        {
            var Q0;
            Q0 = qSketchRegion(id + "F0", true);
            var Q1;
            Q1 = qSketchRegion(id + "F2", true);
            loft(context, id + "F3", {"sheetProfilesArray" : [{ "sheetProfileEntities" : qUnion([Q0]) }, { "sheetProfileEntities" : qUnion([Q1]) }]});
        }
    });
